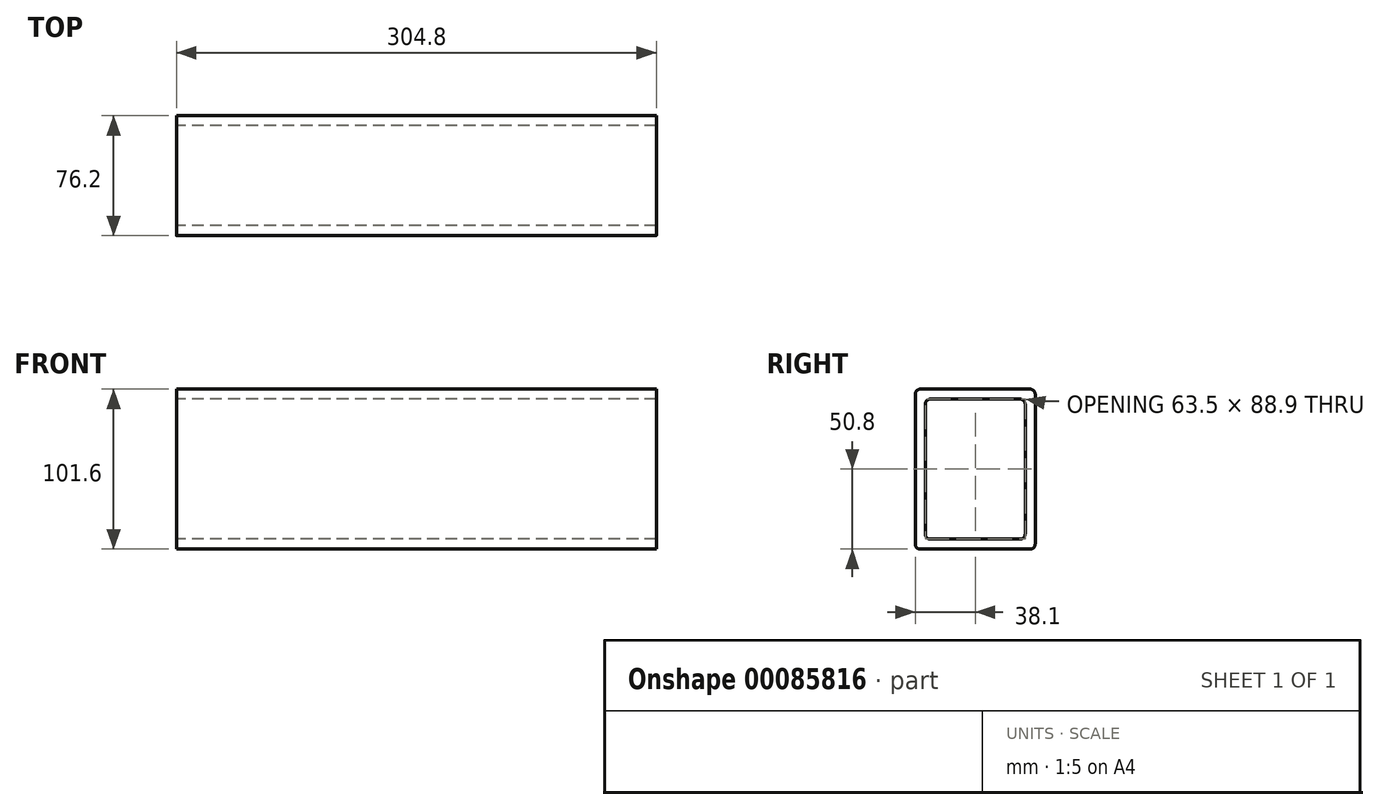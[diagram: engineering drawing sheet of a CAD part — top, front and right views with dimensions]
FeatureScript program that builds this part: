
annotation { "Feature Type Name" : "Feature", "Feature Type Description" : "" }
export const myFeature = defineFeature(function(context is Context, id is Id, definition is map)
    precondition{}
    {
        {
            var Q0;
            Q0=qCreatedBy(makeId("Right.planeOp"),FACE);
            var sketch = newSketch(context, id + "F0", { "sketchPlane" : qUnion([Q0])});
            skLineSegment(sketch, "E0.bottom", {"start": v(-34.92, 50.8) * mm, "end": v(34.93, 50.8) * mm});
            skLineSegment(sketch, "E0.top", {"start": v(-34.93, -50.8) * mm, "end": v(34.92, -50.8) * mm});
            skLineSegment(sketch, "E0.left", {"start": v(-38.1, 47.63) * mm, "end": v(-38.1, -47.62) * mm});
            skLineSegment(sketch, "E0.right", {"start": v(38.1, 47.63) * mm, "end": v(38.1, -47.62) * mm});
            skPoint(sketch, "E0.middle", {"position": v(0, 0) * mm});
            skLineSegment(sketch, "E1.0", {"start": v(-31.75, 41.28) * mm, "end": v(-31.75, -41.27) * mm});
            skLineSegment(sketch, "E2.3", {"start": v(-28.58, -44.45) * mm, "end": v(28.58, -44.45) * mm});
            skLineSegment(sketch, "E3.0", {"start": v(31.75, 41.28) * mm, "end": v(31.75, -41.27) * mm});
            skLineSegment(sketch, "E3.1", {"start": v(-28.58, 44.45) * mm, "end": v(28.58, 44.45) * mm});
            skPoint(sketch, "E4.visualSharp", {"position": v(-38.1, 50.8) * mm});
            skArc(sketch, "E4.filletArc", {"start": v(-34.92, 50.8) * mm, "mid": v(-37.17, 49.87) * mm, "end": v(-38.1, 47.63) * mm});
            skPoint(sketch, "E5.visualSharp", {"position": v(38.1, 50.8) * mm});
            skArc(sketch, "E5.filletArc", {"start": v(38.1, 47.63) * mm, "mid": v(37.17, 49.87) * mm, "end": v(34.93, 50.8) * mm});
            skPoint(sketch, "E6.visualSharp", {"position": v(38.1, -50.8) * mm});
            skArc(sketch, "E6.filletArc", {"start": v(34.92, -50.8) * mm, "mid": v(37.17, -49.87) * mm, "end": v(38.1, -47.62) * mm});
            skPoint(sketch, "E7.visualSharp", {"position": v(-38.1, -50.8) * mm});
            skArc(sketch, "E7.filletArc", {"start": v(-38.1, -47.62) * mm, "mid": v(-37.17, -49.87) * mm, "end": v(-34.93, -50.8) * mm});
            skPoint(sketch, "E8.visualSharp", {"position": v(-31.75, -44.45) * mm});
            skArc(sketch, "E8.filletArc", {"start": v(-31.75, -41.27) * mm, "mid": v(-30.82, -43.52) * mm, "end": v(-28.58, -44.45) * mm});
            skPoint(sketch, "E9.visualSharp", {"position": v(-31.75, 44.45) * mm});
            skArc(sketch, "E9.filletArc", {"start": v(-28.58, 44.45) * mm, "mid": v(-30.82, 43.52) * mm, "end": v(-31.75, 41.28) * mm});
            skPoint(sketch, "E10.visualSharp", {"position": v(31.75, 44.45) * mm});
            skArc(sketch, "E10.filletArc", {"start": v(31.75, 41.28) * mm, "mid": v(30.82, 43.52) * mm, "end": v(28.58, 44.45) * mm});
            skPoint(sketch, "E11.visualSharp", {"position": v(31.75, -44.45) * mm});
            skArc(sketch, "E11.filletArc", {"start": v(28.58, -44.45) * mm, "mid": v(30.82, -43.52) * mm, "end": v(31.75, -41.27) * mm});
            skSolve(sketch);
        }
        {
            var Q0;
            Q0=makeQuery(id+"F0.imprint","IMPRINT",FACE,{"disambiguationData":[TD([[makeQuery(id+"F0.imprint","IMPRINT",EDGE,{"derivedFrom":sQuery(id+"F0.wireOp",EDGE,"E0.bottom")}),-1.0]])]});
            extrude(context, id + "F1", {"entities" : qUnion([Q0]), "depth" : 304.8 * mm, "offsetDistance" : 25.4 * mm});
        }
    });
